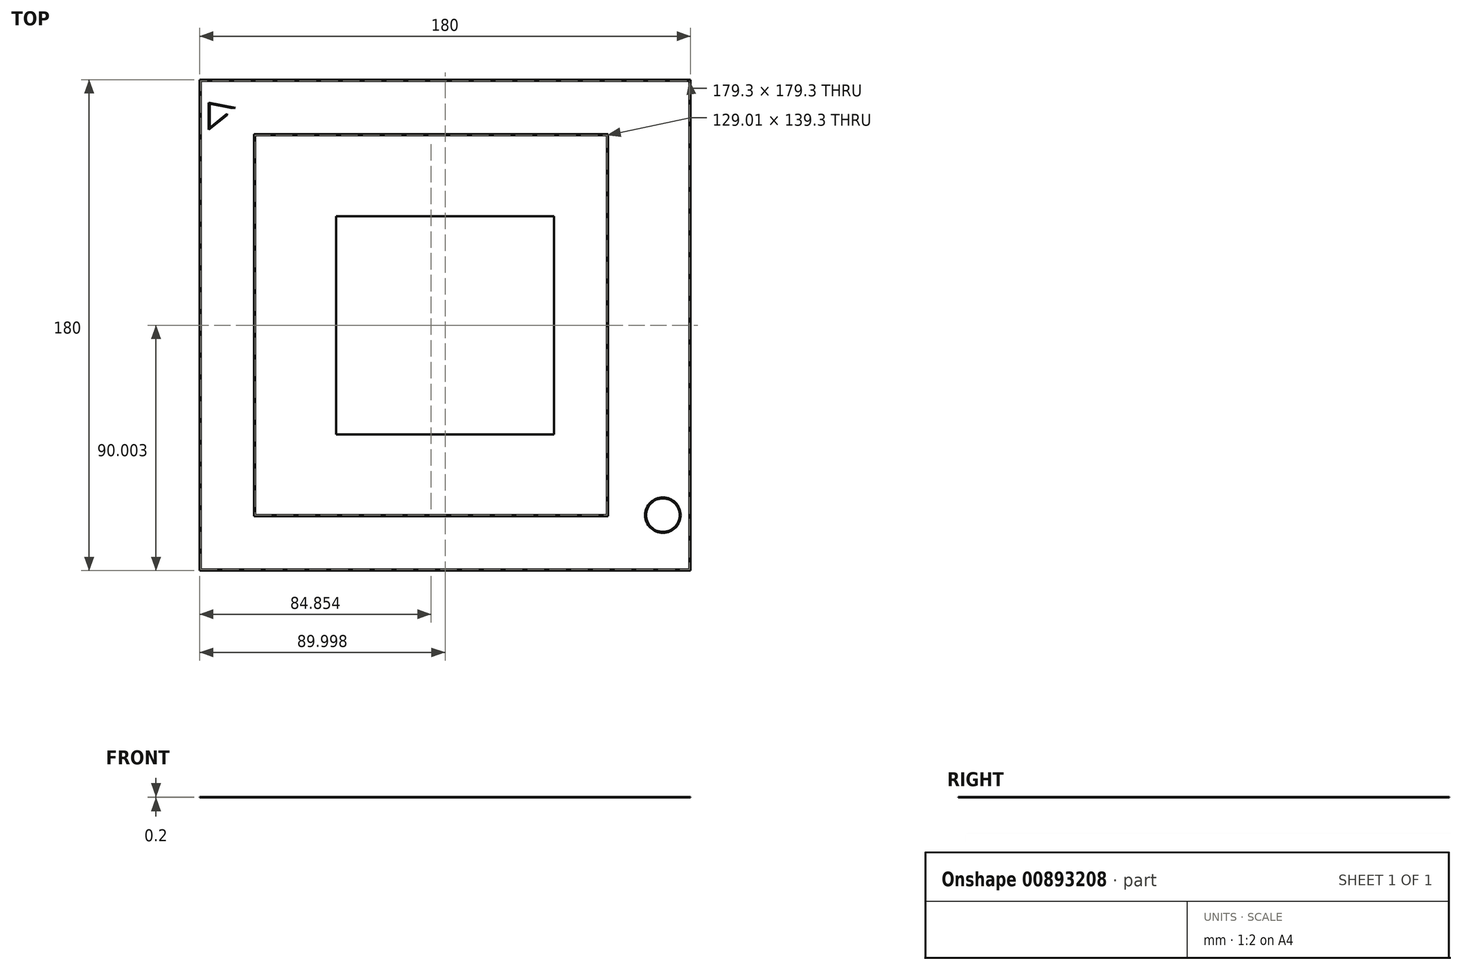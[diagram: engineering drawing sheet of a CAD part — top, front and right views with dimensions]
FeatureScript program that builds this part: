
annotation { "Feature Type Name" : "Feature", "Feature Type Description" : "" }
export const myFeature = defineFeature(function(context is Context, id is Id, definition is map)
    precondition{}
    {
        {
            assignVariable(context, id + "F0", {"name" : "LineHeight", "anyValue" : 0.2});
        }
        {
            var Q0;
            Q0=qCreatedBy(makeId("Top.planeOp"),FACE);
            var sketch = newSketch(context, id + "F1", { "sketchPlane" : qUnion([Q0])});
            skLineSegment(sketch, "E0.bottom", {"start": v(-91.48, 107.86) * mm, "end": v(88.52, 107.86) * mm});
            skLineSegment(sketch, "E0.top", {"start": v(-91.48, -72.14) * mm, "end": v(88.52, -72.14) * mm});
            skLineSegment(sketch, "E0.left", {"start": v(-91.48, 107.86) * mm, "end": v(-91.48, -72.14) * mm});
            skLineSegment(sketch, "E0.right", {"start": v(88.52, 107.86) * mm, "end": v(88.52, -72.14) * mm});
            skLineSegment(sketch, "E1.bottom", {"start": v(-81.48, 97.86) * mm, "end": v(68.23, 97.86) * mm});
            skLineSegment(sketch, "E1.top", {"start": v(-81.48, -62.14) * mm, "end": v(68.23, -62.14) * mm});
            skLineSegment(sketch, "E1.left", {"start": v(-81.48, 97.86) * mm, "end": v(-81.48, -62.14) * mm});
            skLineSegment(sketch, "E1.right", {"start": v(68.23, 97.86) * mm, "end": v(68.23, -62.14) * mm});
            skLineSegment(sketch, "E2.bottom", {"start": v(-71.48, 87.86) * mm, "end": v(58.23, 87.86) * mm});
            skLineSegment(sketch, "E2.top", {"start": v(-71.48, -52.14) * mm, "end": v(58.23, -52.14) * mm});
            skLineSegment(sketch, "E2.left", {"start": v(-71.48, 87.86) * mm, "end": v(-71.48, -52.14) * mm});
            skLineSegment(sketch, "E2.right", {"start": v(58.23, 87.86) * mm, "end": v(58.23, -52.14) * mm});
            skLineSegment(sketch, "E3.bottom", {"start": v(-41.48, 57.86) * mm, "end": v(38.52, 57.86) * mm});
            skLineSegment(sketch, "E3.top", {"start": v(-41.48, -22.14) * mm, "end": v(38.52, -22.14) * mm});
            skLineSegment(sketch, "E3.left", {"start": v(-41.48, 57.86) * mm, "end": v(-41.48, -22.14) * mm});
            skLineSegment(sketch, "E3.right", {"start": v(38.52, 57.86) * mm, "end": v(38.52, -22.14) * mm});
            skLineSegment(sketch, "E4", {"start": v(-88.13, 99.51) * mm, "end": v(-88.13, 89.51) * mm});
            skLineSegment(sketch, "E5", {"start": v(-88.13, 89.51) * mm, "end": v(-78.33, 97.51) * mm});
            skLineSegment(sketch, "E6", {"start": v(-78.33, 97.51) * mm, "end": v(-88.13, 99.51) * mm});
            skCircle(sketch, "E7", {"center": v(78.37, -51.79) * mm, "radius": 6.5 * mm});
            skLineSegment(sketch, "E8", {"start": v(68.23, -51.79) * mm, "end": v(88.52, -51.79) * mm, "construction": true});
            skLineSegment(sketch, "E9", {"start": v(-91.13, 107.51) * mm, "end": v(88.17, 107.51) * mm});
            skLineSegment(sketch, "E10", {"start": v(88.17, 107.51) * mm, "end": v(88.17, -71.79) * mm});
            skLineSegment(sketch, "E11", {"start": v(88.17, -71.79) * mm, "end": v(-91.13, -71.79) * mm});
            skLineSegment(sketch, "E12", {"start": v(-91.13, -71.79) * mm, "end": v(-91.13, 107.51) * mm});
            skLineSegment(sketch, "E13", {"start": v(-81.13, 97.51) * mm, "end": v(67.88, 97.51) * mm});
            skLineSegment(sketch, "E14", {"start": v(67.88, 97.51) * mm, "end": v(67.88, -61.79) * mm});
            skLineSegment(sketch, "E15", {"start": v(67.88, -61.79) * mm, "end": v(-81.13, -61.79) * mm});
            skLineSegment(sketch, "E16", {"start": v(-81.13, -61.79) * mm, "end": v(-81.13, 97.51) * mm});
            skLineSegment(sketch, "E17", {"start": v(-71.13, 87.51) * mm, "end": v(57.88, 87.51) * mm});
            skLineSegment(sketch, "E18", {"start": v(57.88, 87.51) * mm, "end": v(57.88, -51.79) * mm});
            skLineSegment(sketch, "E19", {"start": v(57.88, -51.79) * mm, "end": v(-71.13, -51.79) * mm});
            skLineSegment(sketch, "E20", {"start": v(-71.13, -51.79) * mm, "end": v(-71.13, 87.51) * mm});
            skCircle(sketch, "E21", {"center": v(78.37, -51.79) * mm, "radius": 6.15 * mm});
            skLineSegment(sketch, "E22", {"start": v(-87.78, 99.08) * mm, "end": v(-79.13, 97.32) * mm});
            skPoint(sketch, "E22.startSnap0", {"position": v(-85.71, 99.08) * mm});
            skLineSegment(sketch, "E23", {"start": v(-79.13, 97.32) * mm, "end": v(-87.78, 90.25) * mm});
            skLineSegment(sketch, "E24", {"start": v(-87.78, 90.25) * mm, "end": v(-87.78, 99.08) * mm});
            skSolve(sketch);
        }
        {
            var Q0;
            Q0=makeQuery(id+"F1.imprint","IMPRINT",FACE,{"disambiguationData":[TD([[makeQuery(id+"F1.imprint","IMPRINT",EDGE,{"derivedFrom":sQuery(id+"F1.wireOp",EDGE,"E0.bottom")}),-1.0]])]});
            var Q1;
            Q1=makeQuery(id+"F1.imprint","IMPRINT",FACE,{"disambiguationData":[TD([[makeQuery(id+"F1.imprint","IMPRINT",EDGE,{"derivedFrom":sQuery(id+"F1.wireOp",EDGE,"E1.bottom")}),-1.0]])]});
            var Q2;
            Q2=makeQuery(id+"F1.imprint","IMPRINT",FACE,{"disambiguationData":[TD([[makeQuery(id+"F1.imprint","IMPRINT",EDGE,{"derivedFrom":sQuery(id+"F1.wireOp",EDGE,"E2.bottom")}),-1.0]])]});
            var Q3;
            Q3=makeQuery(id+"F1.imprint","IMPRINT",FACE,{"disambiguationData":[TD([[makeQuery(id+"F1.imprint","IMPRINT",EDGE,{"derivedFrom":sQuery(id+"F1.wireOp",EDGE,"E7")}),1.0]])]});
            var Q4;
            Q4=makeQuery(id+"F1.imprint","IMPRINT",FACE,{"disambiguationData":[TD([[makeQuery(id+"F1.imprint","IMPRINT",EDGE,{"derivedFrom":sQuery(id+"F1.wireOp",EDGE,"E3.bottom")}),-1.0]])]});
            var Q5;
            Q5=makeQuery(id+"F1.imprint","IMPRINT",FACE,{"disambiguationData":[TD([[makeQuery(id+"F1.imprint","IMPRINT",EDGE,{"derivedFrom":sQuery(id+"F1.wireOp",EDGE,"E4")}),1.0]])]});
            extrude(context, id + "F2", {"entities" : qUnion([Q0, Q1, Q2, Q3, Q4, Q5]), "depth" : (getVariable(context, 'LineHeight')) * mm, "offsetDistance" : 25 * mm});
        }
    });
